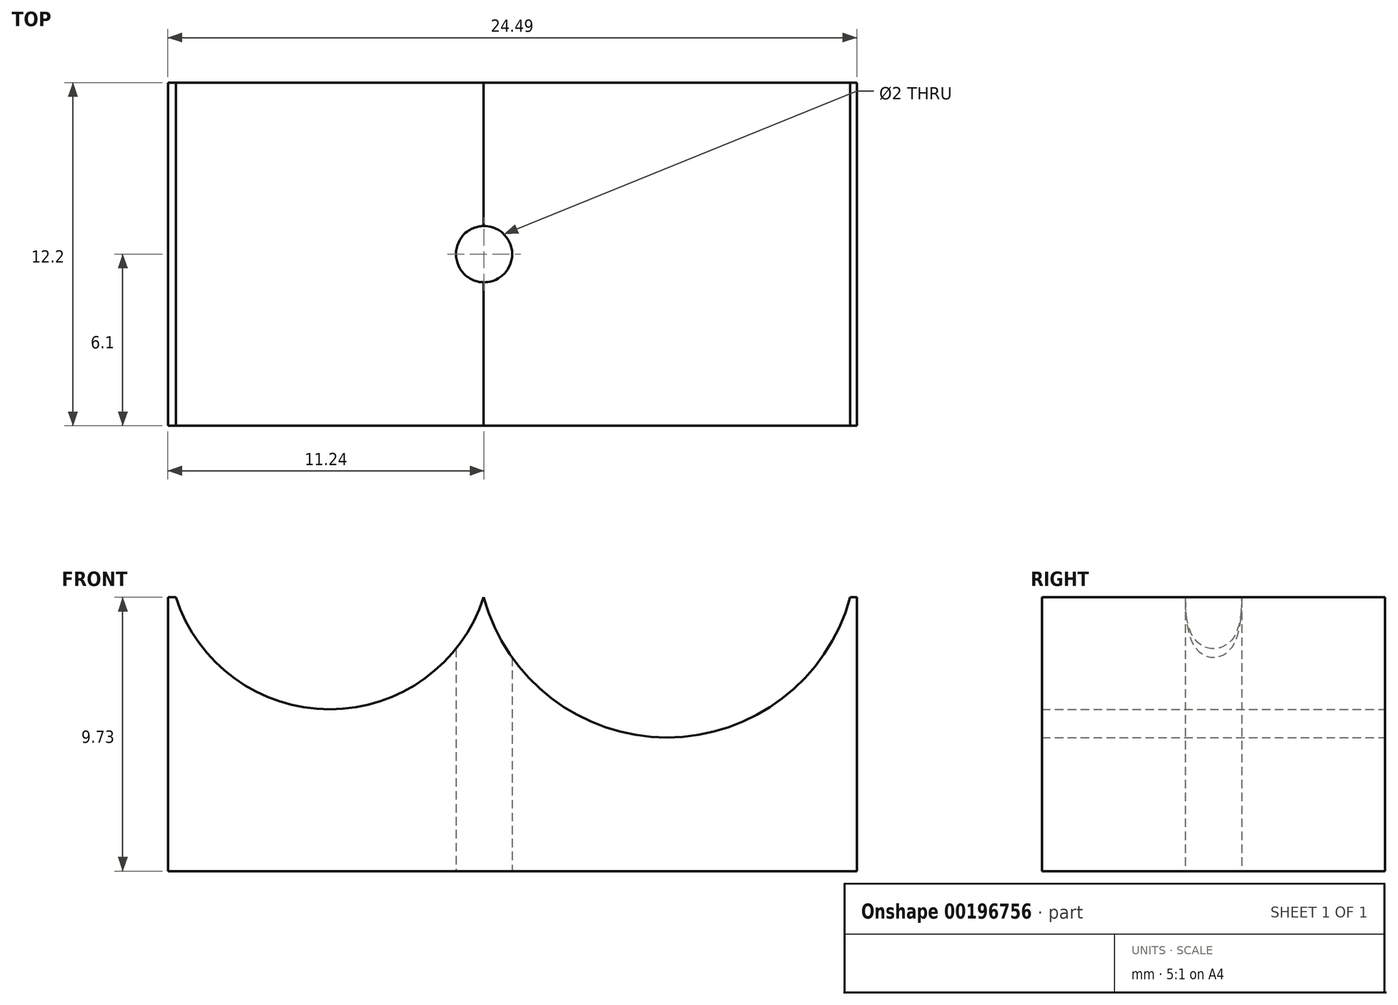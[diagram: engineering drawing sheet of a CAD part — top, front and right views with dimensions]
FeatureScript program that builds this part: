
annotation { "Feature Type Name" : "Feature", "Feature Type Description" : "" }
export const myFeature = defineFeature(function(context is Context, id is Id, definition is map)
    precondition{}
    {
        {
            var Q0;
            Q0=qCreatedBy(makeId("Front.planeOp"),FACE);
            var sketch = newSketch(context, id + "F0", { "sketchPlane" : qUnion([Q0])});
            skLineSegment(sketch, "E0", {"start": v(-48.75, 0) * mm, "end": v(53.74, 0) * mm, "construction": true});
            skLineSegment(sketch, "E1", {"start": v(-48.52, -11.5) * mm, "end": v(53.74, -11.5) * mm, "construction": true});
            skArc(sketch, "E2", {"start": v(-10.96, -1.77) * mm, "mid": v(-5.49, -5.75) * mm, "end": v(-0.01, -1.77) * mm});
            skArc(sketch, "E3", {"start": v(-0.01, -1.77) * mm, "mid": v(6.5, -6.75) * mm, "end": v(13.02, -1.77) * mm});
            skLineSegment(sketch, "E4", {"start": v(-11.24, -1.77) * mm, "end": v(-11.24, -11.5) * mm});
            skLineSegment(sketch, "E5", {"start": v(13.25, -1.77) * mm, "end": v(13.25, -11.5) * mm});
            skLineSegment(sketch, "E6", {"start": v(13.25, -11.5) * mm, "end": v(-11.24, -11.5) * mm});
            skLineSegment(sketch, "E7", {"start": v(-10.96, -1.77) * mm, "end": v(-11.24, -1.77) * mm});
            skLineSegment(sketch, "E8", {"start": v(-11.24, -1.77) * mm, "end": v(-10.96, -1.77) * mm});
            skLineSegment(sketch, "E9.trimOffspring", {"start": v(13.02, -1.77) * mm, "end": v(13.25, -1.77) * mm});
            skSolve(sketch);
        }
        {
            var Q0;
            Q0=makeQuery(id+"F0.imprint","IMPRINT",FACE,{"disambiguationData":[TD([[makeQuery(id+"F0.imprint","IMPRINT",EDGE,{"derivedFrom":sQuery(id+"F0.wireOp",EDGE,"E4")}),1.0]])]});
            extrude(context, id + "F1", {"entities" : qUnion([Q0]), "endBound" : BoundingType.SYMMETRIC, "depth" : 12.2 * mm});
        }
        {
            var Q0;
            Q0=makeQuery(id+"F1.opExtrude","SWEPT_FACE",FACE,{"disambiguationData":[OSD([sQuery(id+"F0.wireOp",EDGE,"E6")])]});
            var sketch = newSketch(context, id + "F2", { "sketchPlane" : qUnion([Q0])});
            skCircle(sketch, "E10", {"center": v(0, 0) * mm, "radius": 1 * mm});
            skLineSegment(sketch, "E11", {"start": v(-0.64, 0.77) * mm, "end": v(0.65, -0.76) * mm});
            skSolve(sketch);
        }
        {
            var Q0;
            {var subQ0=sQuery(id+"F2.wireOp",EDGE,"E11");Q0=makeQuery(id+"F2.imprint","IMPRINT",FACE,{"disambiguationData":[TD([[makeQuery(id+"F2.imprint","IMPRINT",EDGE,{"derivedFrom":subQ0}),1.0]])]});}
            var Q1;
            {var subQ0=sQuery(id+"F2.wireOp",EDGE,"E11");Q1=makeQuery(id+"F2.imprint","IMPRINT",FACE,{"disambiguationData":[TD([[makeQuery(id+"F2.imprint","IMPRINT",EDGE,{"derivedFrom":subQ0}),-1.0]])]});}
            extrude(context, id + "F3", {"entities" : qUnion([Q0, Q1]), "operationType" : NewBodyOperationType.REMOVE, "oppositeDirection" : true, "depth" : 25 * mm});
        }
    });
